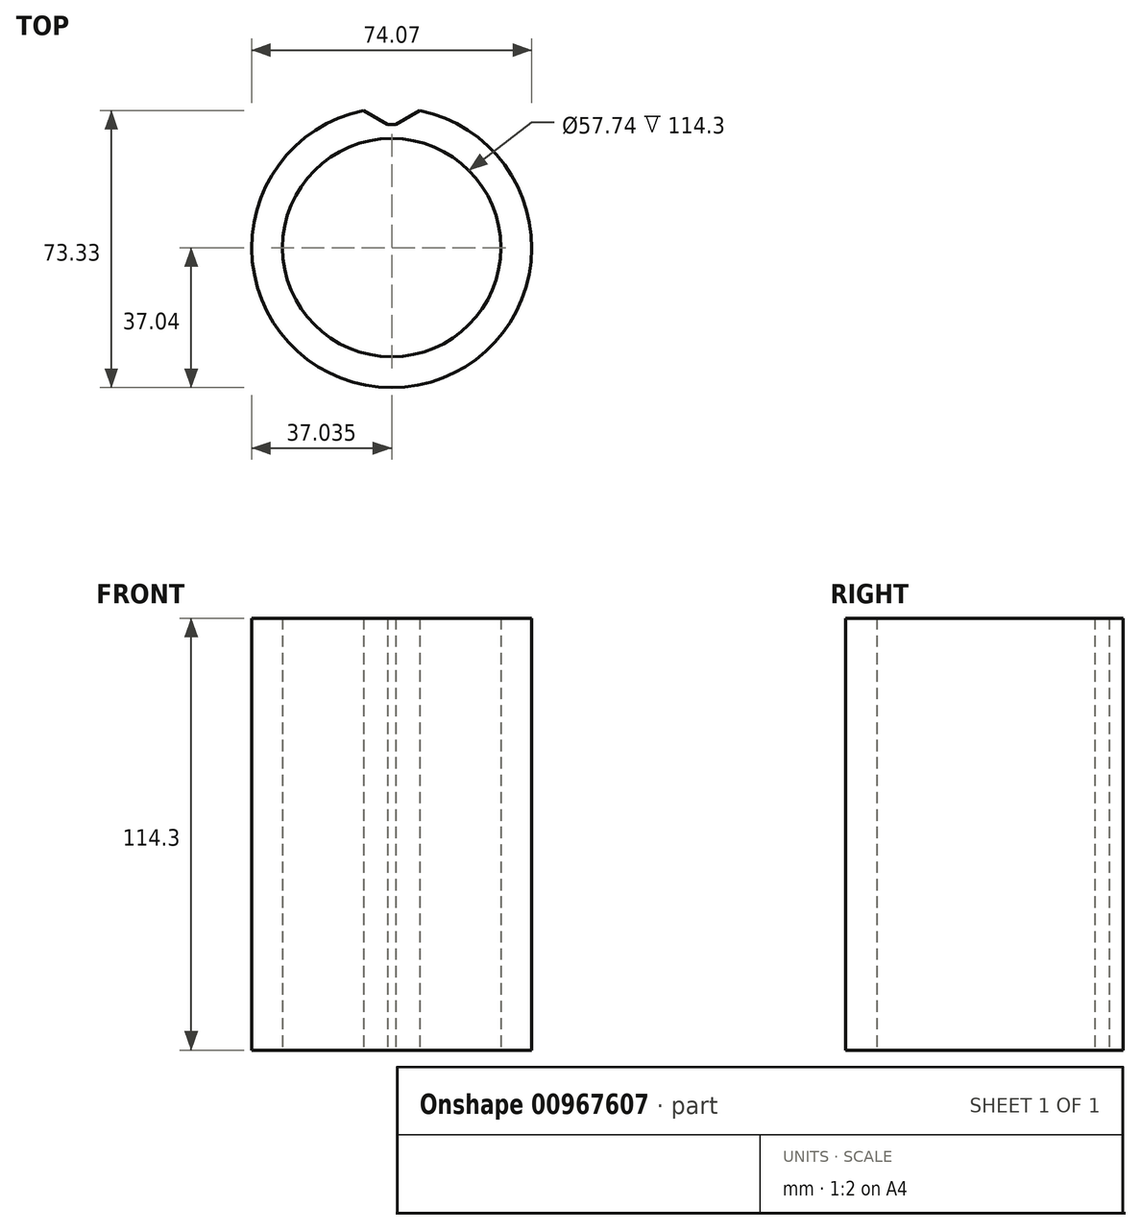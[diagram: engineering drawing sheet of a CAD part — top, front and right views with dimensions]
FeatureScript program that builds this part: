
annotation { "Feature Type Name" : "Feature", "Feature Type Description" : "" }
export const myFeature = defineFeature(function(context is Context, id is Id, definition is map)
    precondition{}
    {
        {
            var Q0;
            Q0=qCreatedBy(makeId("Top.planeOp"),FACE);
            var sketch = newSketch(context, id + "F0", { "sketchPlane" : qUnion([Q0])});
            skArc(sketch, "E0", {"start": v(31.53, 71.26) * mm, "mid": v(24.12, -2.07) * mm, "end": v(16.7, 71.26) * mm});
            skCircle(sketch, "E1", {"center": v(24.12, 34.97) * mm, "radius": 28.87 * mm});
            skArc(sketch, "E2", {"start": v(25.19, 67.58) * mm, "mid": v(24.12, 67.6) * mm, "end": v(23.04, 67.58) * mm});
            skLineSegment(sketch, "E3", {"start": v(16.7, 71.26) * mm, "end": v(23.04, 67.58) * mm});
            skLineSegment(sketch, "E4", {"start": v(31.53, 71.26) * mm, "end": v(25.19, 67.58) * mm});
            skPoint(sketch, "E5.start.orphan", {"position": v(24.12, 85.55) * mm});
            skSolve(sketch);
        }
        {
            var Q0;
            Q0=makeQuery(id+"F0.imprint","IMPRINT",FACE,{"disambiguationData":[TD([[makeQuery(id+"F0.imprint","IMPRINT",EDGE,{"derivedFrom":sQuery(id+"F0.wireOp",EDGE,"E0")}),-1.0]])]});
            var Q1;
            Q1 = qSketchRegion(id + "F0", true);
            extrude(context, id + "F1", {"entities" : qUnion([Q0, Q1]), "depth" : 114.3 * mm, "offsetDistance" : 25.4 * mm});
        }
    });
